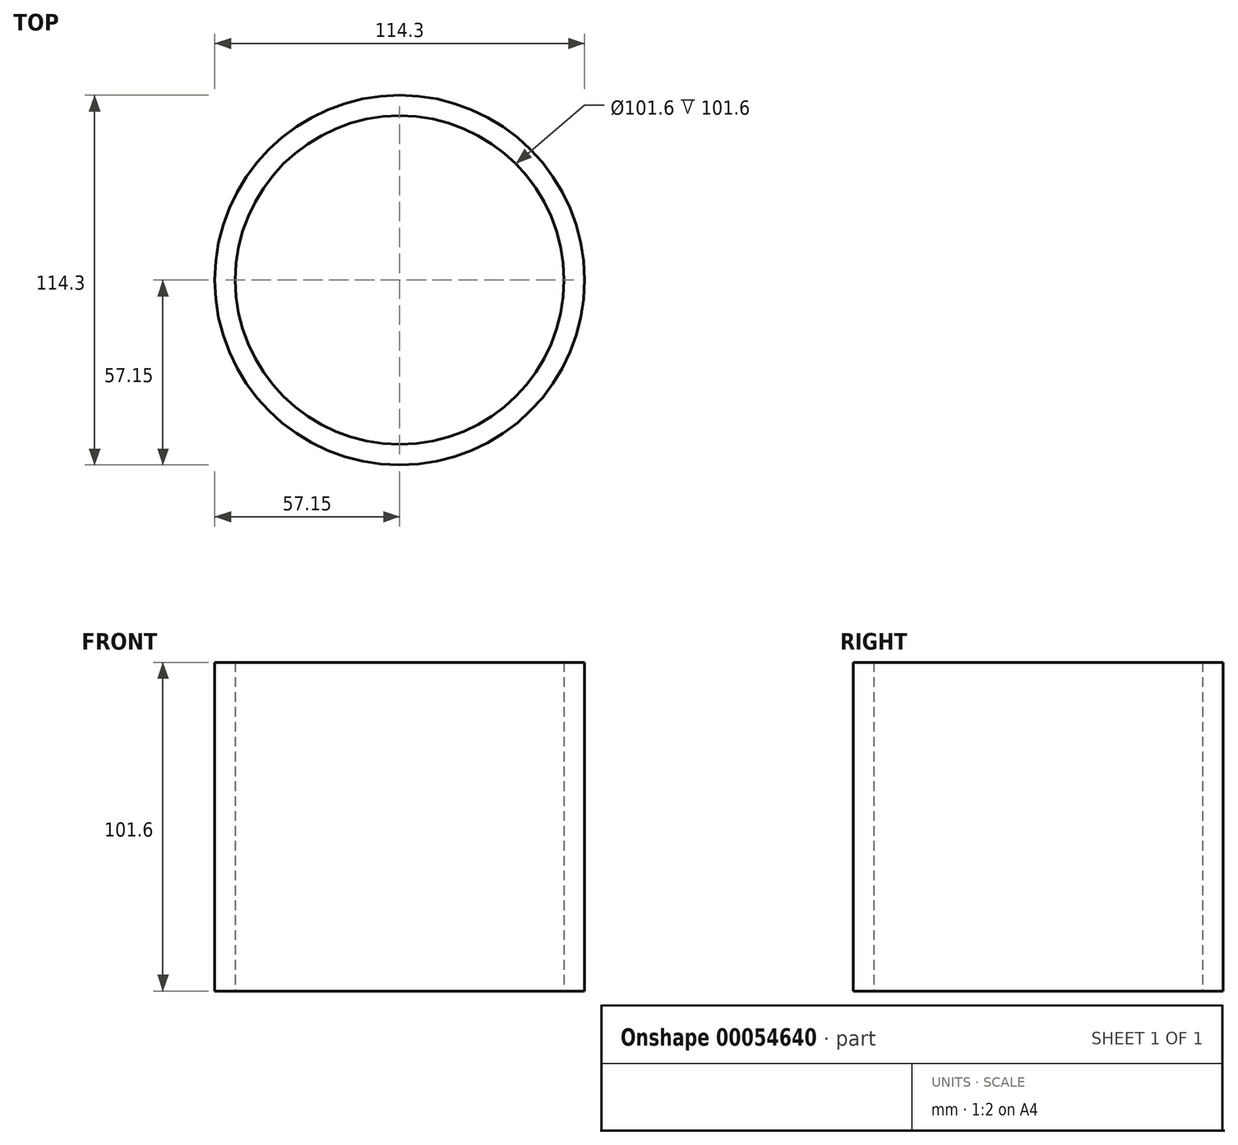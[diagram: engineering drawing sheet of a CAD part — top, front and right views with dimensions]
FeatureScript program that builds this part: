
annotation { "Feature Type Name" : "Feature", "Feature Type Description" : "" }
export const myFeature = defineFeature(function(context is Context, id is Id, definition is map)
    precondition{}
    {
        {
            var Q0;
            Q0=qCreatedBy(makeId("Top.planeOp"),FACE);
            var sketch = newSketch(context, id + "F0", { "sketchPlane" : qUnion([Q0])});
            skCircle(sketch, "E0", {"center": v(0, 0) * mm, "radius": 57.15 * mm});
            skCircle(sketch, "E1", {"center": v(0, 0) * mm, "radius": 50.8 * mm});
            skSolve(sketch);
        }
        {
            var Q0;
            Q0 = qSketchRegion(id + "F0", true);
            extrude(context, id + "F1", {"entities" : qUnion([Q0]), "depth" : 101.6 * mm});
        }
    });
